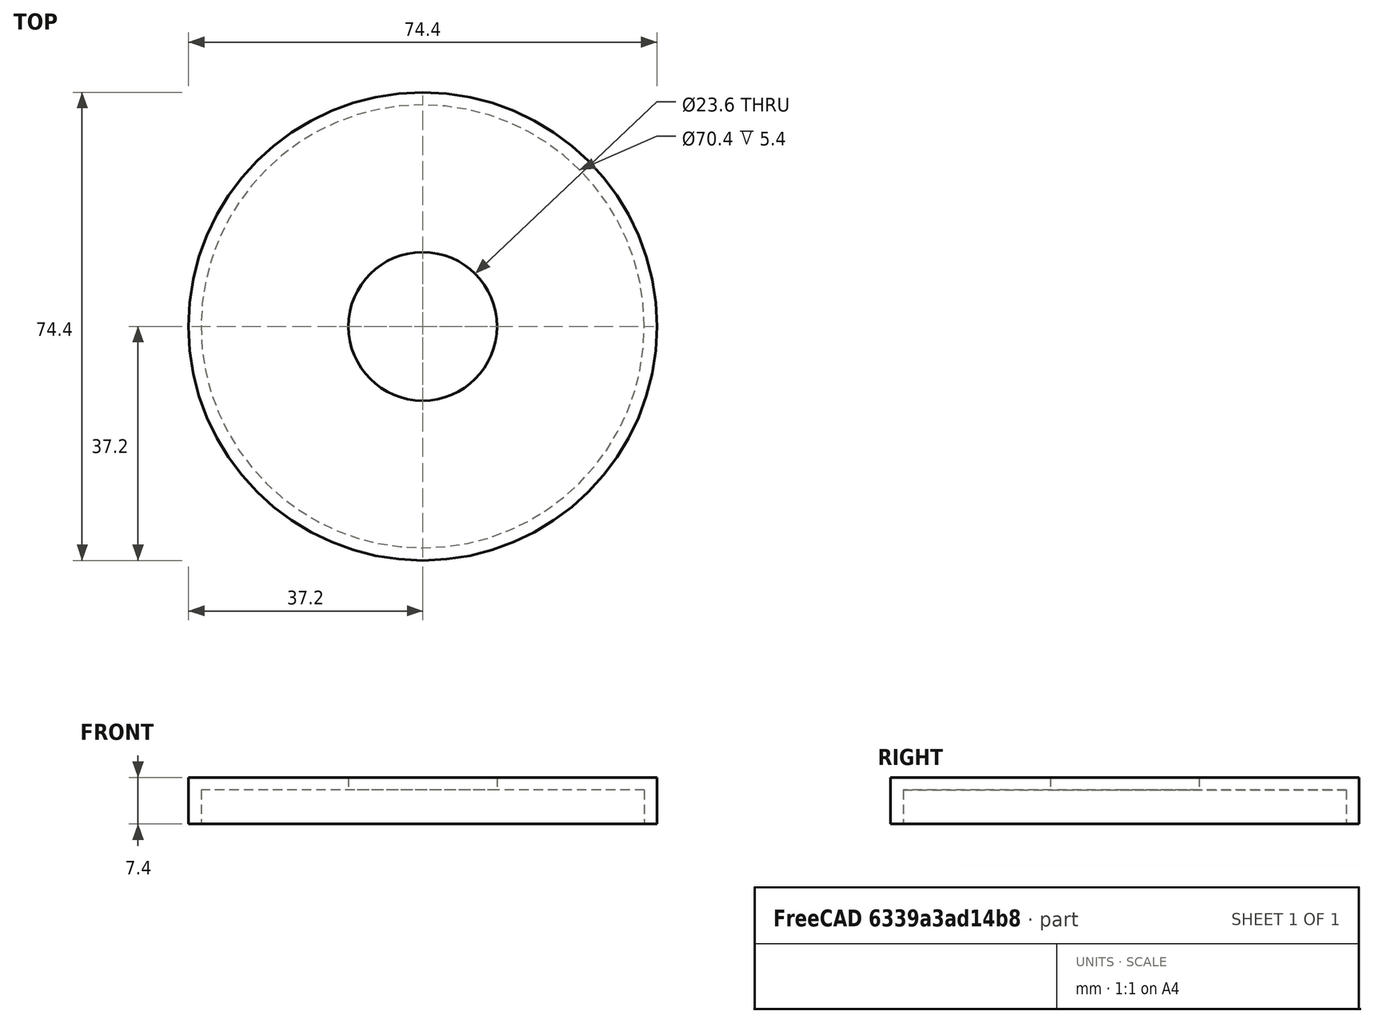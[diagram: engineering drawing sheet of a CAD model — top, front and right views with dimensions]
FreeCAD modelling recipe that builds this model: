
FCSTD DOCUMENT  (FreeCAD 0.18R16117 (Git))
Label: Scheibe
License: All rights reserved
LicenseURL: http://en.wikipedia.org/wiki/All_rights_reserved
objects: Sketcher::SketchObject×1, PartDesign::Revolution×1, PartDesign::Body×1
note: 4 computed .brp shape members not serialized (recipe doc carries the construction recipe); baked Part::Feature solids carry a one-line shape summary decoded from their .brp

FEATURE [Sketcher::SketchObject] Sketch
  MapMode = 5
  Placement = pos=(0,0,0) rot=(1,0,0;1.5708rad)
  Support = -> [XZ_Plane]
  sketch-geometry (6):
    g0: LineSegment StartX=11.8 StartY=7.4 StartZ=0 EndX=11.8 EndY=5.4 EndZ=0
    g1: LineSegment StartX=11.8 StartY=5.4 StartZ=0 EndX=35.2 EndY=5.4 EndZ=0
    g2: LineSegment StartX=35.2 StartY=5.4 StartZ=0 EndX=35.2 EndY=0 EndZ=0
    g3: LineSegment StartX=35.2 StartY=0 StartZ=0 EndX=37.2 EndY=0 EndZ=0
    g4: LineSegment StartX=37.2 StartY=0 StartZ=0 EndX=37.2 EndY=7.4 EndZ=0
    g5: LineSegment StartX=11.8 StartY=7.4 StartZ=0 EndX=37.2 EndY=7.4 EndZ=0
  constraints (18):
    c: Coincident(g0,g1)
    c: Horizontal(g1)
    c: Coincident(g1,g2)
    c: Vertical(g2)
    c: Coincident(g2,g3)
    c: Horizontal(g3)
    c: Coincident(g3,g4)
    c: Vertical(g4)
    c: PointOnObject(g2,g-1)
    c: Horizontal(g5)
    c: DistanceX(g-1,g3) = 37.2
    c: Vertical(g0)
    c: DistanceY(g0,g0) = 2
    c: Coincident(g5,g4)
    c: DistanceY(g4,g4) = 7.4
    c: Coincident(g0,g5)
    c: Equal(g0,g3)
    c: DistanceX(g-1,g0) = 11.8
FEATURE [PartDesign::Revolution] Revolution
  Angle = 360
  Axis = (0,-1.035e-13,1)
  Base = (0,0,0)
  Placement = pos=(0,0,0) rot=(1,0,0;1.5708rad)
  Profile = -> Sketch
  ReferenceAxis = -> Sketch [V_Axis]
  Reversed = true
FEATURE [PartDesign::Body] Body
  Group = -> [Sketch,Revolution]
  Origin = -> Origin
  Tip = -> Revolution
